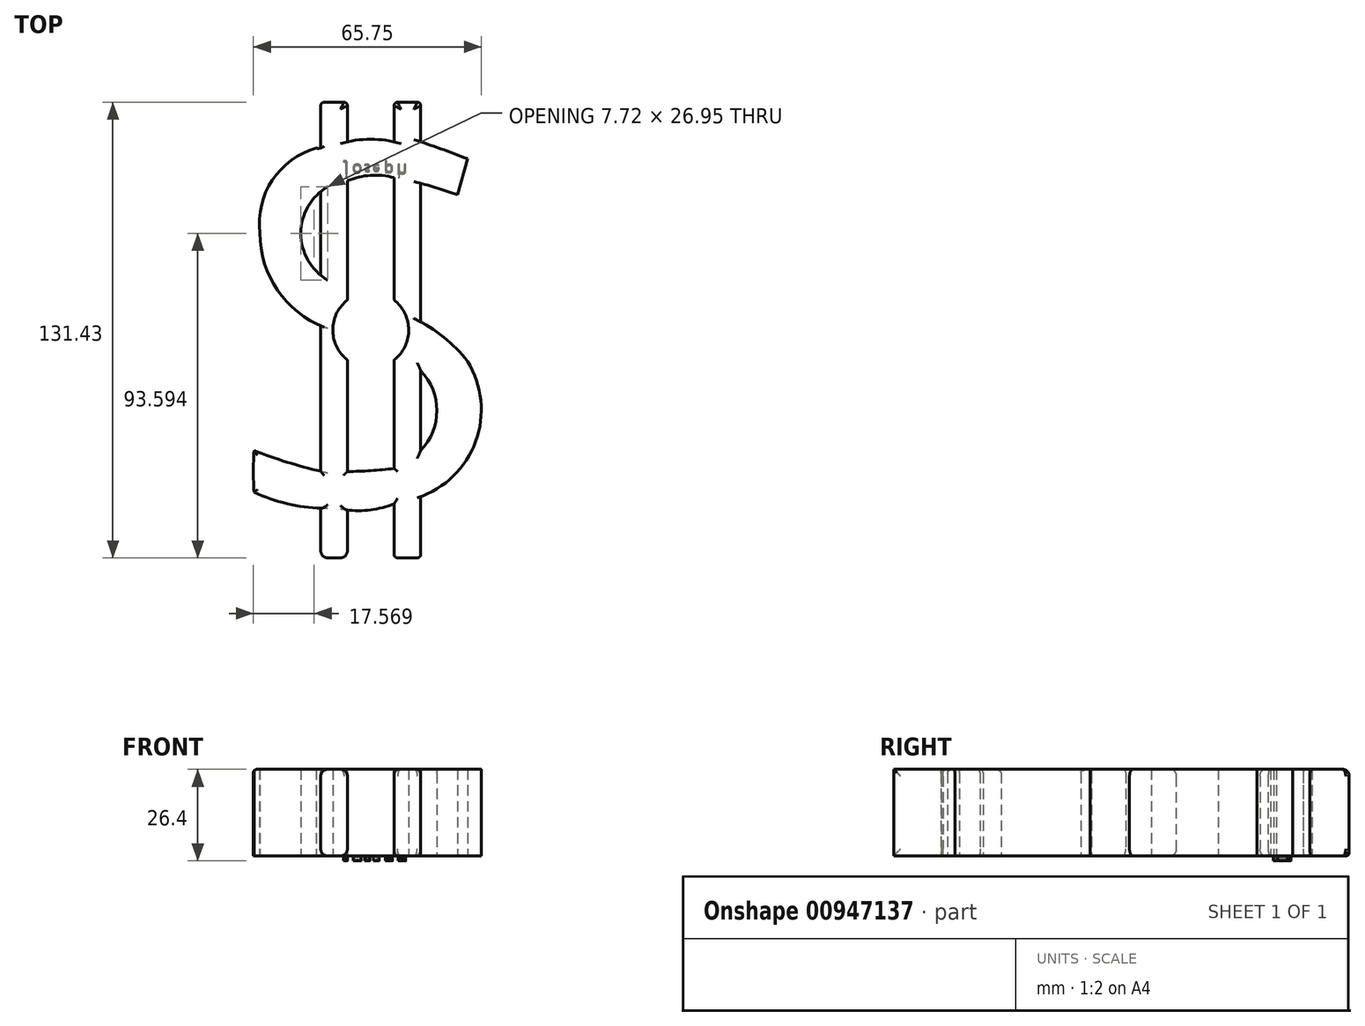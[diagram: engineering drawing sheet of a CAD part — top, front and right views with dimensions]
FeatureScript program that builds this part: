
annotation { "Feature Type Name" : "Feature", "Feature Type Description" : "" }
export const myFeature = defineFeature(function(context is Context, id is Id, definition is map)
    precondition{}
    {
        {
            var Q0;
            Q0=qCreatedBy(makeId("Top.planeOp"),FACE);
            var sketch = newSketch(context, id + "F0", { "sketchPlane" : qUnion([Q0])});
            skLineSegment(sketch, "E0.bottom", {"start": v(-6.73, 76.15) * mm, "end": v(-14.43, 76.15) * mm});
            skLineSegment(sketch, "E0.top", {"start": v(-6.73, -55.28) * mm, "end": v(-14.43, -55.28) * mm});
            skLineSegment(sketch, "E0.left", {"start": v(-6.73, 76.15) * mm, "end": v(-6.73, 19.07) * mm});
            skLineSegment(sketch, "E0.right", {"start": v(-14.43, 76.15) * mm, "end": v(-14.43, -55.28) * mm});
            skLineSegment(sketch, "E1.MirrorCS", {"start": v(14.43, 76.15) * mm, "end": v(14.43, -55.28) * mm});
            skLineSegment(sketch, "E2.MirrorCS", {"start": v(6.73, 76.15) * mm, "end": v(6.73, 19.07) * mm});
            skLineSegment(sketch, "E3.MirrorCS", {"start": v(6.73, 76.15) * mm, "end": v(14.43, 76.15) * mm});
            skLineSegment(sketch, "E4.MirrorCS", {"start": v(6.73, -55.28) * mm, "end": v(14.43, -55.28) * mm});
            skPoint(sketch, "E5", {"position": v(-6.73, 10.43) * mm});
            skPoint(sketch, "E6.end.orphan", {"position": v(0, 10.43) * mm});
            skCircle(sketch, "E7", {"center": v(0, 10.43) * mm, "radius": 10.95 * mm});
            skLineSegment(sketch, "E8.trimOffspring", {"start": v(-6.73, 1.8) * mm, "end": v(-6.73, -55.28) * mm});
            skLineSegment(sketch, "E9.trimOffspring", {"start": v(6.73, 1.8) * mm, "end": v(6.73, -55.28) * mm});
            skArc(sketch, "E10", {"start": v(25, 49.5) * mm, "mid": v(19.74, 51.21) * mm, "end": v(14.43, 52.77) * mm});
            skArc(sketch, "E11", {"start": v(6.73, 54.4) * mm, "mid": v(-0.07, 55.07) * mm, "end": v(-6.73, 53.5) * mm});
            skArc(sketch, "E12", {"start": v(-14.43, 50.4) * mm, "mid": v(-20.15, 38.31) * mm, "end": v(-14.43, 26.23) * mm});
            skArc(sketch, "E13", {"start": v(-4.56, 20.39) * mm, "mid": v(-5.6, 20.98) * mm, "end": v(-6.73, 21.32) * mm});
            skArc(sketch, "E14", {"start": v(27.96, 1.4) * mm, "mid": v(19.9, 9.29) * mm, "end": v(10.05, 14.79) * mm});
            skArc(sketch, "E15", {"start": v(14.43, -37.62) * mm, "mid": v(30.42, -21.31) * mm, "end": v(27.96, 1.4) * mm});
            skArc(sketch, "E16", {"start": v(-6.73, -41.5) * mm, "mid": v(0.11, -41.42) * mm, "end": v(6.73, -39.68) * mm});
            skArc(sketch, "E17", {"start": v(-33.67, -36.32) * mm, "mid": v(-24.28, -39.62) * mm, "end": v(-14.43, -40.98) * mm});
            skArc(sketch, "E18", {"start": v(-33.67, -24.3) * mm, "mid": v(-33.86, -30.31) * mm, "end": v(-33.67, -36.32) * mm});
            skArc(sketch, "E19", {"start": v(-33.67, -24.3) * mm, "mid": v(-24.16, -27.68) * mm, "end": v(-14.43, -30.31) * mm});
            skPoint(sketch, "E19.endSnap0", {"position": v(-33.86, -30.31) * mm});
            skArc(sketch, "E20", {"start": v(-6.73, -30.38) * mm, "mid": v(0.01, -30.14) * mm, "end": v(6.73, -29.47) * mm});
            skArc(sketch, "E21", {"start": v(14.43, -24.3) * mm, "mid": v(19.08, -12.8) * mm, "end": v(14.43, -1.3) * mm});
            skArc(sketch, "E22", {"start": v(8.13, 3.1) * mm, "mid": v(11.12, 0.67) * mm, "end": v(14.43, -1.3) * mm});
            skArc(sketch, "E23", {"start": v(-31.99, 38.38) * mm, "mid": v(-26.13, 20.9) * mm, "end": v(-10.95, 10.43) * mm});
            skPoint(sketch, "E23.endSnap0", {"position": v(-14.43, 10.43) * mm});
            skArc(sketch, "E24", {"start": v(-15.7, 62.93) * mm, "mid": v(-28.38, 53.67) * mm, "end": v(-31.99, 38.38) * mm});
            skArc(sketch, "E25", {"start": v(-15.7, 62.93) * mm, "mid": v(-15.07, 62.85) * mm, "end": v(-14.43, 62.93) * mm});
            skArc(sketch, "E26", {"start": v(6.73, 64.74) * mm, "mid": v(0, 65.48) * mm, "end": v(-6.73, 64.74) * mm});
            skArc(sketch, "E27", {"start": v(27.96, 59.83) * mm, "mid": v(21.22, 62.36) * mm, "end": v(14.43, 64.74) * mm});
            skLineSegment(sketch, "E28", {"start": v(27.96, 59.83) * mm, "end": v(25, 49.5) * mm});
            skSolve(sketch);
        }
        {
            var Q0;
            Q0 = qSketchRegion(id + "F0", true);
            extrude(context, id + "F1", {"entities" : qUnion([Q0]), "depth" : 25 * mm, "offsetDistance" : 25 * mm});
        }
        {
            var Q0;
            {var subQ0=sQuery(id+"F0.wireOp",EDGE,"E0.right");Q0=makeQuery(id+"F1.opExtrude","CAP_EDGE",EDGE,{"disambiguationData":[OSD([subQ0]),TDD([makeQuery(id+"F0.imprint","IMPRINT",EDGE,{"disambiguationData":[TD([[makeQuery(id+"F0.imprint","INTERSECT",VERTEX,{"derivedFrom":[sQuery(id+"F0.wireOp",EDGE,"E0.bottom"),subQ0]}),-1.0]])],"derivedFrom":subQ0})])],"isStart":false});}
            var Q1;
            Q1=makeQuery(id+"F1.opExtrude","SWEPT_EDGE",EDGE,{"disambiguationData":[OSD([sQuery(id+"F0.wireOp",EDGE,"E0.bottom"),sQuery(id+"F0.wireOp",EDGE,"E0.right")])]});
            var Q2;
            Q2=makeQuery(id+"F1.opExtrude","SWEPT_EDGE",EDGE,{"disambiguationData":[OSD([sQuery(id+"F0.wireOp",EDGE,"E0.bottom"),sQuery(id+"F0.wireOp",EDGE,"E0.left")])]});
            var Q3;
            Q3=makeQuery(id+"F1.opExtrude","SWEPT_EDGE",EDGE,{"disambiguationData":[OSD([sQuery(id+"F0.wireOp",EDGE,"E1.MirrorCS"),sQuery(id+"F0.wireOp",EDGE,"E3.MirrorCS")])]});
            var Q4;
            Q4=makeQuery(id+"F1.opExtrude","SWEPT_EDGE",EDGE,{"disambiguationData":[OSD([sQuery(id+"F0.wireOp",EDGE,"E2.MirrorCS"),sQuery(id+"F0.wireOp",EDGE,"E3.MirrorCS")])]});
            var Q5;
            Q5=makeQuery(id+"F1.opExtrude","SWEPT_EDGE",EDGE,{"disambiguationData":[OSD([sQuery(id+"F0.wireOp",EDGE,"E1.MirrorCS"),sQuery(id+"F0.wireOp",EDGE,"E4.MirrorCS")])]});
            var Q6;
            Q6=makeQuery(id+"F1.opExtrude","SWEPT_EDGE",EDGE,{"disambiguationData":[OSD([sQuery(id+"F0.wireOp",EDGE,"E4.MirrorCS"),sQuery(id+"F0.wireOp",EDGE,"E9.trimOffspring")])]});
            var Q7;
            {var subQ0=sQuery(id+"F0.wireOp",EDGE,"E9.trimOffspring");Q7=makeQuery(id+"F1.opExtrude","CAP_EDGE",EDGE,{"disambiguationData":[OSD([subQ0]),TDD([makeQuery(id+"F0.imprint","IMPRINT",EDGE,{"disambiguationData":[TD([[makeQuery(id+"F0.imprint","INTERSECT",VERTEX,{"derivedFrom":[sQuery(id+"F0.wireOp",EDGE,"E4.MirrorCS"),subQ0]}),1.0]])],"derivedFrom":subQ0})])],"isStart":false});}
            var Q8;
            {var subQ0=sQuery(id+"F0.wireOp",EDGE,"E1.MirrorCS");Q8=makeQuery(id+"F1.opExtrude","CAP_EDGE",EDGE,{"disambiguationData":[OSD([subQ0]),TDD([makeQuery(id+"F0.imprint","IMPRINT",EDGE,{"disambiguationData":[TD([[makeQuery(id+"F0.imprint","INTERSECT",VERTEX,{"derivedFrom":[subQ0,sQuery(id+"F0.wireOp",EDGE,"E4.MirrorCS")]}),1.0]])],"derivedFrom":subQ0})])],"isStart":false});}
            var Q9;
            {var subQ0=sQuery(id+"F0.wireOp",EDGE,"E21");var subQ1=sQuery(id+"F0.wireOp",EDGE,"E1.MirrorCS");Q9=makeQuery(id+"F1.opExtrude","CAP_EDGE",EDGE,{"disambiguationData":[OSD([subQ1]),TDD([makeQuery(id+"F0.imprint","IMPRINT",EDGE,{"disambiguationData":[TD([[makeQuery(id+"F0.imprint","INTERSECT",VERTEX,{"derivedFrom":[subQ1,subQ0]}),1.0]])],"derivedFrom":subQ1})])],"isStart":false});}
            var Q10;
            {var subQ0=sQuery(id+"F0.wireOp",EDGE,"E9.trimOffspring");Q10=makeQuery(id+"F1.opExtrude","CAP_EDGE",EDGE,{"disambiguationData":[OSD([subQ0]),TDD([makeQuery(id+"F0.imprint","IMPRINT",EDGE,{"disambiguationData":[TD([[makeQuery(id+"F0.imprint","INTERSECT",VERTEX,{"derivedFrom":[sQuery(id+"F0.wireOp",EDGE,"E7"),subQ0]}),-1.0]])],"derivedFrom":subQ0})])],"isStart":false});}
            var Q11;
            {var subQ0=sQuery(id+"F0.wireOp",EDGE,"E0.right");Q11=makeQuery(id+"F1.opExtrude","CAP_EDGE",EDGE,{"disambiguationData":[OSD([subQ0]),TDD([makeQuery(id+"F0.imprint","IMPRINT",EDGE,{"disambiguationData":[TD([[makeQuery(id+"F0.imprint","INTERSECT",VERTEX,{"derivedFrom":[subQ0,sQuery(id+"F0.wireOp",EDGE,"E19")]}),1.0]])],"derivedFrom":subQ0})])],"isStart":false});}
            var Q12;
            {var subQ0=sQuery(id+"F0.wireOp",EDGE,"E8.trimOffspring");Q12=makeQuery(id+"F1.opExtrude","CAP_EDGE",EDGE,{"disambiguationData":[OSD([subQ0]),TDD([makeQuery(id+"F0.imprint","IMPRINT",EDGE,{"disambiguationData":[TD([[makeQuery(id+"F0.imprint","INTERSECT",VERTEX,{"derivedFrom":[sQuery(id+"F0.wireOp",EDGE,"E7"),subQ0]}),-1.0]])],"derivedFrom":subQ0})])],"isStart":false});}
            var Q13;
            Q13=makeQuery(id+"F1.opExtrude","CAP_EDGE",EDGE,{"disambiguationData":[OSD([sQuery(id+"F0.wireOp",EDGE,"E16")])],"isStart":false});
            var Q14;
            Q14=makeQuery(id+"F1.opExtrude","CAP_EDGE",EDGE,{"disambiguationData":[OSD([sQuery(id+"F0.wireOp",EDGE,"E20")])],"isStart":false});
            var Q15;
            Q15=makeQuery(id+"F1.opExtrude","CAP_EDGE",EDGE,{"disambiguationData":[OSD([sQuery(id+"F0.wireOp",EDGE,"E19")])],"isStart":false});
            var Q16;
            Q16=makeQuery(id+"F1.opExtrude","CAP_EDGE",EDGE,{"disambiguationData":[OSD([sQuery(id+"F0.wireOp",EDGE,"E18")])],"isStart":false});
            var Q17;
            Q17=makeQuery(id+"F1.opExtrude","CAP_EDGE",EDGE,{"disambiguationData":[OSD([sQuery(id+"F0.wireOp",EDGE,"E17")])],"isStart":false});
            var Q18;
            Q18=makeQuery(id+"F1.opExtrude","CAP_EDGE",EDGE,{"disambiguationData":[OSD([sQuery(id+"F0.wireOp",EDGE,"E21")])],"isStart":false});
            fillet(context, id + "F2", {"entities" : qUnion([Q0, Q1, Q2, Q3, Q4, Q5, Q6, Q7, Q8, Q9, Q10, Q11, Q12, Q13, Q14, Q15, Q16, Q17, Q18]), "radius" : 1 * mm, "tangentPropagation" : true, "allowEdgeOverflow" : false});
        }
        {
            var Q0;
            Q0=makeQuery(id+"F1.opExtrude","CAP_EDGE",EDGE,{"disambiguationData":[OSD([sQuery(id+"F0.wireOp",EDGE,"E15")])],"isStart":false});
            var Q1;
            Q1=makeQuery(id+"F1.opExtrude","CAP_EDGE",EDGE,{"disambiguationData":[OSD([sQuery(id+"F0.wireOp",EDGE,"E14")])],"isStart":false});
            fillet(context, id + "F3", {"entities" : qUnion([Q0, Q1]), "radius" : 0.02 * mm, "tangentPropagation" : true, "allowEdgeOverflow" : false});
        }
        {
            var Q0;
            {var subQ0=sQuery(id+"F0.wireOp",EDGE,"E1.MirrorCS");Q0=makeQuery(id+"F1.opExtrude","CAP_EDGE",EDGE,{"disambiguationData":[OSD([subQ0]),TDD([makeQuery(id+"F0.imprint","IMPRINT",EDGE,{"disambiguationData":[TD([[makeQuery(id+"F0.imprint","INTERSECT",VERTEX,{"derivedFrom":[subQ0,sQuery(id+"F0.wireOp",EDGE,"E10")]}),-1.0]])],"derivedFrom":subQ0})])],"isStart":false});}
            var Q1;
            {var subQ0=sQuery(id+"F0.wireOp",EDGE,"E1.MirrorCS");Q1=makeQuery(id+"F1.opExtrude","CAP_EDGE",EDGE,{"disambiguationData":[OSD([subQ0]),TDD([makeQuery(id+"F0.imprint","IMPRINT",EDGE,{"disambiguationData":[TD([[makeQuery(id+"F0.imprint","INTERSECT",VERTEX,{"derivedFrom":[subQ0,sQuery(id+"F0.wireOp",EDGE,"E10")]}),-1.0]])],"derivedFrom":subQ0})])],"isStart":true});}
            var Q2;
            Q2=makeQuery(id+"F1.opExtrude","CAP_EDGE",EDGE,{"disambiguationData":[OSD([sQuery(id+"F0.wireOp",EDGE,"E0.bottom")])],"isStart":false});
            var Q3;
            Q3=makeQuery(id+"F1.opExtrude","CAP_EDGE",EDGE,{"disambiguationData":[OSD([sQuery(id+"F0.wireOp",EDGE,"E3.MirrorCS")])],"isStart":false});
            var Q4;
            Q4=makeQuery(id+"F1.opExtrude","CAP_EDGE",EDGE,{"disambiguationData":[OSD([sQuery(id+"F0.wireOp",EDGE,"E3.MirrorCS")])],"isStart":true});
            fillet(context, id + "F4", {"entities" : qUnion([Q0, Q1, Q2, Q3, Q4]), "radius" : 2 * mm, "tangentPropagation" : true, "allowEdgeOverflow" : false});
        }
        {
            var Q0;
            {var subQ0=sQuery(id+"F0.wireOp",EDGE,"E12");var subQ1=sQuery(id+"F0.wireOp",EDGE,"E0.right");Q0=makeQuery(id+"F1.opExtrude","CAP_EDGE",EDGE,{"disambiguationData":[OSD([subQ1]),TDD([makeQuery(id+"F0.imprint","IMPRINT",EDGE,{"disambiguationData":[TD([[makeQuery(id+"F0.imprint","INTERSECT",VERTEX,{"disambiguationData":[OD(0.0)],"derivedFrom":[subQ1,subQ0]}),-1.0]])],"derivedFrom":subQ1})])],"isStart":true});}
            var Q1;
            {var subQ0=sQuery(id+"F0.wireOp",EDGE,"E0.right");Q1=makeQuery(id+"F1.opExtrude","CAP_EDGE",EDGE,{"disambiguationData":[OSD([subQ0]),TDD([makeQuery(id+"F0.imprint","IMPRINT",EDGE,{"disambiguationData":[TD([[makeQuery(id+"F0.imprint","INTERSECT",VERTEX,{"derivedFrom":[subQ0,sQuery(id+"F0.wireOp",EDGE,"E19")]}),1.0]])],"derivedFrom":subQ0})])],"isStart":true});}
            var Q2;
            {var subQ0=sQuery(id+"F0.wireOp",EDGE,"E12");var subQ1=sQuery(id+"F0.wireOp",EDGE,"E0.right");Q2=makeQuery(id+"F1.opExtrude","CAP_EDGE",EDGE,{"disambiguationData":[OSD([subQ1]),TDD([makeQuery(id+"F0.imprint","IMPRINT",EDGE,{"disambiguationData":[TD([[makeQuery(id+"F0.imprint","INTERSECT",VERTEX,{"disambiguationData":[OD(0.0)],"derivedFrom":[subQ1,subQ0]}),-1.0]])],"derivedFrom":subQ1})])],"isStart":false});}
            var Q3;
            {var subQ0=sQuery(id+"F0.wireOp",EDGE,"E0.right");Q3=makeQuery(id+"F1.opExtrude","CAP_EDGE",EDGE,{"disambiguationData":[OSD([subQ0]),TDD([makeQuery(id+"F0.imprint","IMPRINT",EDGE,{"disambiguationData":[TD([[makeQuery(id+"F0.imprint","INTERSECT",VERTEX,{"derivedFrom":[sQuery(id+"F0.wireOp",EDGE,"E0.top"),subQ0]}),1.0]])],"derivedFrom":subQ0})])],"isStart":false});}
            var Q4;
            {var subQ0=sQuery(id+"F0.wireOp",EDGE,"E8.trimOffspring");Q4=makeQuery(id+"F1.opExtrude","CAP_EDGE",EDGE,{"disambiguationData":[OSD([subQ0]),TDD([makeQuery(id+"F0.imprint","IMPRINT",EDGE,{"disambiguationData":[TD([[makeQuery(id+"F0.imprint","INTERSECT",VERTEX,{"derivedFrom":[sQuery(id+"F0.wireOp",EDGE,"E0.top"),subQ0]}),1.0]])],"derivedFrom":subQ0})])],"isStart":false});}
            var Q5;
            Q5=makeQuery(id+"F1.opExtrude","SWEPT_EDGE",EDGE,{"disambiguationData":[OSD([sQuery(id+"F0.wireOp",EDGE,"E0.top"),sQuery(id+"F0.wireOp",EDGE,"E0.right")])]});
            var Q6;
            Q6=makeQuery(id+"F1.opExtrude","SWEPT_EDGE",EDGE,{"disambiguationData":[OSD([sQuery(id+"F0.wireOp",EDGE,"E0.top"),sQuery(id+"F0.wireOp",EDGE,"E8.trimOffspring")])]});
            var Q7;
            {var subQ0=sQuery(id+"F0.wireOp",EDGE,"E0.right");Q7=makeQuery(id+"F1.opExtrude","CAP_EDGE",EDGE,{"disambiguationData":[OSD([subQ0]),TDD([makeQuery(id+"F0.imprint","IMPRINT",EDGE,{"disambiguationData":[TD([[makeQuery(id+"F0.imprint","INTERSECT",VERTEX,{"derivedFrom":[sQuery(id+"F0.wireOp",EDGE,"E0.top"),subQ0]}),1.0]])],"derivedFrom":subQ0})])],"isStart":true});}
            var Q8;
            {var subQ0=sQuery(id+"F0.wireOp",EDGE,"E8.trimOffspring");Q8=makeQuery(id+"F1.opExtrude","CAP_EDGE",EDGE,{"disambiguationData":[OSD([subQ0]),TDD([makeQuery(id+"F0.imprint","IMPRINT",EDGE,{"disambiguationData":[TD([[makeQuery(id+"F0.imprint","INTERSECT",VERTEX,{"derivedFrom":[sQuery(id+"F0.wireOp",EDGE,"E0.top"),subQ0]}),1.0]])],"derivedFrom":subQ0})])],"isStart":true});}
            fillet(context, id + "F5", {"entities" : qUnion([Q0, Q1, Q2, Q3, Q4, Q5, Q6, Q7, Q8]), "radius" : 2 * mm, "tangentPropagation" : true, "allowEdgeOverflow" : false});
        }
        {
            var Q0;
            {var subQ0=sQuery(id+"F0.wireOp",EDGE,"E0.right");Q0=makeQuery(id+"F1.opExtrude","CAP_EDGE",EDGE,{"disambiguationData":[OSD([subQ0]),TDD([makeQuery(id+"F0.imprint","IMPRINT",EDGE,{"disambiguationData":[TD([[makeQuery(id+"F0.imprint","INTERSECT",VERTEX,{"derivedFrom":[sQuery(id+"F0.wireOp",EDGE,"E0.bottom"),subQ0]}),-1.0]])],"derivedFrom":subQ0})])],"isStart":true});}
            var Q1;
            {var subQ0=sQuery(id+"F0.wireOp",EDGE,"E0.left");Q1=makeQuery(id+"F1.opExtrude","CAP_EDGE",EDGE,{"disambiguationData":[OSD([subQ0]),TDD([makeQuery(id+"F0.imprint","IMPRINT",EDGE,{"disambiguationData":[TD([[makeQuery(id+"F0.imprint","INTERSECT",VERTEX,{"derivedFrom":[sQuery(id+"F0.wireOp",EDGE,"E0.bottom"),subQ0]}),-1.0]])],"derivedFrom":subQ0})])],"isStart":true});}
            fillet(context, id + "F6", {"entities" : qUnion([Q0, Q1]), "radius" : 1 * mm, "tangentPropagation" : true, "allowEdgeOverflow" : false});
        }
        {
            var Q0;
            Q0=makeQuery(id+"F1.opExtrude","CAP_FACE",FACE,{"disambiguationData":[OSD([sQuery(id+"F0.wireOp",EDGE,"E0.bottom"),sQuery(id+"F0.wireOp",EDGE,"E0.top"),sQuery(id+"F0.wireOp",EDGE,"E0.left"),sQuery(id+"F0.wireOp",EDGE,"E0.right"),sQuery(id+"F0.wireOp",EDGE,"E1.MirrorCS"),sQuery(id+"F0.wireOp",EDGE,"E2.MirrorCS"),sQuery(id+"F0.wireOp",EDGE,"E3.MirrorCS"),sQuery(id+"F0.wireOp",EDGE,"E4.MirrorCS"),sQuery(id+"F0.wireOp",EDGE,"E7"),sQuery(id+"F0.wireOp",EDGE,"E8.trimOffspring"),sQuery(id+"F0.wireOp",EDGE,"E9.trimOffspring"),sQuery(id+"F0.wireOp",EDGE,"E10"),sQuery(id+"F0.wireOp",EDGE,"E11"),sQuery(id+"F0.wireOp",EDGE,"E12"),sQuery(id+"F0.wireOp",EDGE,"E14"),sQuery(id+"F0.wireOp",EDGE,"E15"),sQuery(id+"F0.wireOp",EDGE,"E16"),sQuery(id+"F0.wireOp",EDGE,"E17"),sQuery(id+"F0.wireOp",EDGE,"E18"),sQuery(id+"F0.wireOp",EDGE,"E19"),sQuery(id+"F0.wireOp",EDGE,"E20"),sQuery(id+"F0.wireOp",EDGE,"E21"),sQuery(id+"F0.wireOp",EDGE,"E23"),sQuery(id+"F0.wireOp",EDGE,"E24"),sQuery(id+"F0.wireOp",EDGE,"E25"),sQuery(id+"F0.wireOp",EDGE,"E26"),sQuery(id+"F0.wireOp",EDGE,"E27"),sQuery(id+"F0.wireOp",EDGE,"E28")])],"isStart":true});
            var sketch = newSketch(context, id + "F7", { "sketchPlane" : qUnion([Q0])});
            skText(sketch, "E29", { "text": "j\n", "fontName": "OpenSans-Regular.ttf"});
            skText(sketch, "E30", { "text": "e", "fontName": "OpenSans-Regular.ttf"});
            skPoint(sketch, "E30.firstSnap0", {"position": v(0.52, -65.47) * mm});
            skText(sketch, "E31", { "text": "p", "fontName": "OpenSans-Regular.ttf"});
            skText(sketch, "E32", { "text": "o", "fontName": "OpenSans-Regular.ttf"});
            skText(sketch, "E33", { "text": "s", "fontName": "OpenSans-Regular.ttf"});
            skText(sketch, "E34", { "text": "h", "fontName": "OpenSans-Regular.ttf"});
            const initialGuessF7  = {"E29": [-0.00762, -0.05805, 1, 0, 0.00367], "E30": [0.00052, -0.05818, 1, 0, 0.00267], "E31": [0.00388, -0.0582, 1, 0, 0.00313], "E32": [-0.00533, -0.05827, 1, 0, 0.00335], "E33": [-0.0019, -0.0582, 1, 0, 0.00276], "E34": [0.0074, -0.05825, 1, 0, 0.00366]};
            skSetInitialGuess(sketch, initialGuessF7);
            skSolve(sketch);
        }
        {
            var Q0;
            Q0 = qSketchRegion(id + "F7", true);
            extrude(context, id + "F8", {"entities" : qUnion([Q0]), "operationType" : NewBodyOperationType.ADD, "depth" : 1.4 * mm, "offsetDistance" : 25 * mm});
        }
    });
